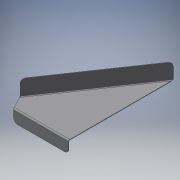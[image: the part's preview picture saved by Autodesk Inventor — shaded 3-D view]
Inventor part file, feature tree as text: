
AUTODESK INVENTOR PART (.ipt)
format: ipt  version: 2018 (Build 220112000, 112)  size: 195,584 bytes
history: native  units: mm
features: sheet_metal_op x7, other x4, sketch x3, fillet x1
ambient origin geometry x8: Origin, YZ Plane, XZ Plane, XY Plane, X Axis, Y Axis, Z Axis, Center Point
bodies: Solid1 (feature_tree)
feature tree (15):
  sheet_metal_op  "Face1"
  sheet_metal_op  "Flange1"
  sheet_metal_op  "Flange2"
  fillet  "Fillet1"  Radius=280.0mm
  sketch  "Sketch1"  dims[d2=9.721484mm]
  other  "Plate1"
  sketch  "Sketch2"  dims[d3=3.0mm]
  other  "Plate2"
  sheet_metal_op  "Bend1"
  sheet_metal_op  "Corner1"
  sketch  "Sketch3"  dims[d4=3.0mm d5=1.5mm d6=6.0mm d7=3.75mm d8=46.0mm d9=90.0deg d10=3.75mm d11=12.0mm d12=3.0mm d13=3.75mm d14=535.98483mm d15=80.0mm d16=4.860742mm d17=40.0mm d18=20.0mm d19=3.0mm d20=1.5mm d21=6.0mm d22=3.75mm d23=41.0mm d24=90.0deg d25=3.75mm d26=12.0mm d27=3.0mm d28=3.75mm]
  other  "Plate3"
  sheet_metal_op  "Bend2"
  sheet_metal_op  "Corner2"
  other  "Definition1"
